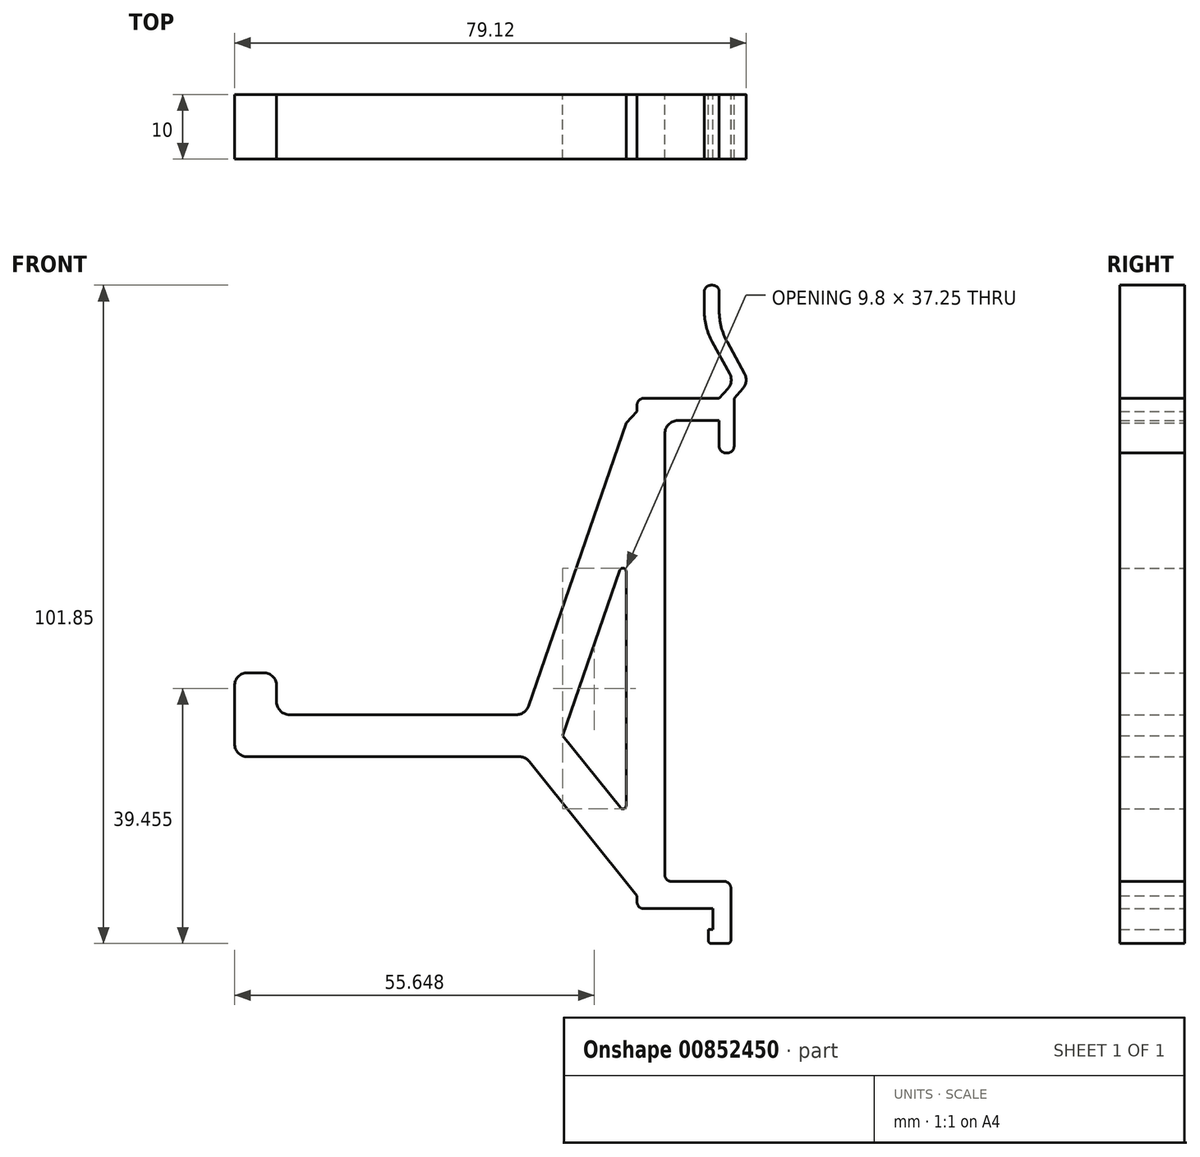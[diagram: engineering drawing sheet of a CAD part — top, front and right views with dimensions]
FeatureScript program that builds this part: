
annotation { "Feature Type Name" : "Feature", "Feature Type Description" : "" }
export const myFeature = defineFeature(function(context is Context, id is Id, definition is map)
    precondition{}
    {
        {
            var Q0;
            Q0=qCreatedBy(makeId("Front.planeOp"),FACE);
            var sketch = newSketch(context, id + "F0", { "sketchPlane" : qUnion([Q0])});
            skLineSegment(sketch, "E0", {"start": v(-6, -23.42) * mm, "end": v(-6, 12.84) * mm});
            skLineSegment(sketch, "E1", {"start": v(-6, 35.78) * mm, "end": v(-4.3, 37.6) * mm});
            skLineSegment(sketch, "E2", {"start": v(-4.3, 37.6) * mm, "end": v(-4.3, 38.6) * mm});
            skLineSegment(sketch, "E3", {"start": v(-3.3, 39.6) * mm, "end": v(8.4, 39.6) * mm});
            skLineSegment(sketch, "E4", {"start": v(10.7, 39.6) * mm, "end": v(10.7, 32.15) * mm});
            skLineSegment(sketch, "E5", {"start": v(9.7, 31.15) * mm, "end": v(9.4, 31.15) * mm});
            skLineSegment(sketch, "E6", {"start": v(8.4, 32.15) * mm, "end": v(8.4, 36.15) * mm});
            skLineSegment(sketch, "E7", {"start": v(8.4, 36.15) * mm, "end": v(2, 36.15) * mm});
            skLineSegment(sketch, "E8", {"start": v(0, 34.15) * mm, "end": v(0, -34.15) * mm});
            skLineSegment(sketch, "E9", {"start": v(1, -35.15) * mm, "end": v(9.2, -35.15) * mm});
            skLineSegment(sketch, "E10", {"start": v(10.2, -36.15) * mm, "end": v(10.2, -44.25) * mm});
            skLineSegment(sketch, "E11", {"start": v(9.7, -44.75) * mm, "end": v(7.2, -44.75) * mm});
            skLineSegment(sketch, "E12", {"start": v(6.7, -44.25) * mm, "end": v(6.7, -42.55) * mm});
            skLineSegment(sketch, "E13", {"start": v(6.7, -42.55) * mm, "end": v(7.45, -42.55) * mm});
            skLineSegment(sketch, "E14", {"start": v(7.45, -42.55) * mm, "end": v(7.45, -39.35) * mm});
            skLineSegment(sketch, "E15", {"start": v(7.45, -39.35) * mm, "end": v(-3.3, -39.35) * mm});
            skLineSegment(sketch, "E16", {"start": v(-4.3, -38.35) * mm, "end": v(-4.3, -37.35) * mm});
            skLineSegment(sketch, "E17", {"start": v(8.4, 56.1) * mm, "end": v(8.4, 53.14) * mm});
            skLineSegment(sketch, "E18", {"start": v(9.63, 48.34) * mm, "end": v(12.32, 43.41) * mm});
            skLineSegment(sketch, "E19", {"start": v(12.06, 41.12) * mm, "end": v(10.7, 39.6) * mm});
            skLineSegment(sketch, "E20", {"start": v(7.4, 57.1) * mm, "end": v(7.1, 57.1) * mm});
            skLineSegment(sketch, "E21", {"start": v(6.1, 56.1) * mm, "end": v(6.1, 53.14) * mm});
            skLineSegment(sketch, "E22", {"start": v(7.33, 48.34) * mm, "end": v(10.02, 43.41) * mm});
            skLineSegment(sketch, "E23", {"start": v(9.76, 41.12) * mm, "end": v(8.4, 39.6) * mm});
            skPoint(sketch, "E24.visualSharp", {"position": v(6.1, 50.58) * mm});
            skArc(sketch, "E24.filletArc", {"start": v(6.1, 53.14) * mm, "mid": v(6.41, 50.66) * mm, "end": v(7.33, 48.34) * mm});
            skPoint(sketch, "E25.visualSharp", {"position": v(8.4, 50.58) * mm});
            skArc(sketch, "E25.filletArc", {"start": v(8.4, 53.14) * mm, "mid": v(8.71, 50.66) * mm, "end": v(9.63, 48.34) * mm});
            skPoint(sketch, "E26.visualSharp", {"position": v(10.7, 42.17) * mm});
            skArc(sketch, "E26.filletArc", {"start": v(9.76, 41.12) * mm, "mid": v(10.25, 42.22) * mm, "end": v(10.02, 43.41) * mm});
            skPoint(sketch, "E27.visualSharp", {"position": v(13, 42.17) * mm});
            skArc(sketch, "E27.filletArc", {"start": v(12.06, 41.12) * mm, "mid": v(12.55, 42.22) * mm, "end": v(12.32, 43.41) * mm});
            skPoint(sketch, "E28.visualSharp", {"position": v(8.4, 57.1) * mm});
            skArc(sketch, "E28.filletArc", {"start": v(8.4, 56.1) * mm, "mid": v(8.1, 56.8) * mm, "end": v(7.4, 57.1) * mm});
            skPoint(sketch, "E29.visualSharp", {"position": v(6.1, 57.1) * mm});
            skArc(sketch, "E29.filletArc", {"start": v(7.1, 57.1) * mm, "mid": v(6.4, 56.8) * mm, "end": v(6.1, 56.1) * mm});
            skPoint(sketch, "E30.visualSharp", {"position": v(10.7, 31.15) * mm});
            skArc(sketch, "E30.filletArc", {"start": v(9.7, 31.15) * mm, "mid": v(10.4, 31.44) * mm, "end": v(10.7, 32.15) * mm});
            skPoint(sketch, "E31.visualSharp", {"position": v(8.4, 31.15) * mm});
            skArc(sketch, "E31.filletArc", {"start": v(8.4, 32.15) * mm, "mid": v(8.7, 31.44) * mm, "end": v(9.4, 31.15) * mm});
            skPoint(sketch, "E32.visualSharp", {"position": v(-4.3, 39.6) * mm});
            skArc(sketch, "E32.filletArc", {"start": v(-3.3, 39.6) * mm, "mid": v(-4, 39.3) * mm, "end": v(-4.3, 38.6) * mm});
            skPoint(sketch, "E33.visualSharp", {"position": v(-4.3, -39.35) * mm});
            skArc(sketch, "E33.filletArc", {"start": v(-4.3, -38.35) * mm, "mid": v(-4, -39.06) * mm, "end": v(-3.3, -39.35) * mm});
            skPoint(sketch, "E34.visualSharp", {"position": v(10.2, -35.15) * mm});
            skArc(sketch, "E34.filletArc", {"start": v(10.2, -36.15) * mm, "mid": v(9.9, -35.44) * mm, "end": v(9.2, -35.15) * mm});
            skLineSegment(sketch, "E35", {"start": v(-6, 35.78) * mm, "end": v(-21.09, -8) * mm});
            skLineSegment(sketch, "E36", {"start": v(-22.98, -9.35) * mm, "end": v(-58.05, -9.35) * mm});
            skLineSegment(sketch, "E37", {"start": v(-64.55, -15.85) * mm, "end": v(-22.5, -15.85) * mm});
            skLineSegment(sketch, "E38", {"start": v(-20.95, -16.6) * mm, "end": v(-4.3, -37.35) * mm});
            skLineSegment(sketch, "E39", {"start": v(-15.8, -12.63) * mm, "end": v(-6.97, 13) * mm});
            skLineSegment(sketch, "E40", {"start": v(-15.8, -12.63) * mm, "end": v(-6.89, -23.74) * mm});
            skLineSegment(sketch, "E41.top", {"start": v(-64.55, -2.85) * mm, "end": v(-62.05, -2.85) * mm});
            skLineSegment(sketch, "E41.left", {"start": v(-66.55, -13.85) * mm, "end": v(-66.55, -4.85) * mm});
            skLineSegment(sketch, "E41.right", {"start": v(-60.05, -7.35) * mm, "end": v(-60.05, -4.85) * mm});
            skPoint(sketch, "E42.visualSharp", {"position": v(-66.55, -15.85) * mm});
            skArc(sketch, "E42.filletArc", {"start": v(-66.55, -13.85) * mm, "mid": v(-65.96, -15.26) * mm, "end": v(-64.55, -15.85) * mm});
            skPoint(sketch, "E43.visualSharp", {"position": v(-60.05, -9.35) * mm});
            skArc(sketch, "E43.filletArc", {"start": v(-60.05, -7.35) * mm, "mid": v(-59.46, -8.76) * mm, "end": v(-58.05, -9.35) * mm});
            skPoint(sketch, "E44.visualSharp", {"position": v(-60.05, -2.85) * mm});
            skArc(sketch, "E44.filletArc", {"start": v(-60.05, -4.85) * mm, "mid": v(-60.64, -3.44) * mm, "end": v(-62.05, -2.85) * mm});
            skPoint(sketch, "E45.visualSharp", {"position": v(-66.55, -2.85) * mm});
            skArc(sketch, "E45.filletArc", {"start": v(-64.55, -2.85) * mm, "mid": v(-65.96, -3.44) * mm, "end": v(-66.55, -4.85) * mm});
            skPoint(sketch, "E46.visualSharp", {"position": v(-21.55, -9.35) * mm});
            skArc(sketch, "E46.filletArc", {"start": v(-22.98, -9.35) * mm, "mid": v(-21.82, -8.98) * mm, "end": v(-21.09, -8) * mm});
            skPoint(sketch, "E47.visualSharp", {"position": v(-21.55, -15.85) * mm});
            skArc(sketch, "E47.filletArc", {"start": v(-20.95, -16.6) * mm, "mid": v(-21.64, -16.05) * mm, "end": v(-22.5, -15.85) * mm});
            skPoint(sketch, "E48.visualSharp", {"position": v(-6, -24.84) * mm});
            skArc(sketch, "E48.filletArc", {"start": v(-6.89, -23.74) * mm, "mid": v(-6.33, -23.9) * mm, "end": v(-6, -23.42) * mm});
            skPoint(sketch, "E49.visualSharp", {"position": v(-6, 15.83) * mm});
            skArc(sketch, "E49.filletArc", {"start": v(-6, 12.84) * mm, "mid": v(-6.42, 13.33) * mm, "end": v(-6.97, 13) * mm});
            skPoint(sketch, "E50.visualSharp", {"position": v(0, -35.15) * mm});
            skArc(sketch, "E50.filletArc", {"start": v(0, -34.15) * mm, "mid": v(0.3, -34.86) * mm, "end": v(1, -35.15) * mm});
            skPoint(sketch, "E51.visualSharp", {"position": v(0, 36.15) * mm});
            skArc(sketch, "E51.filletArc", {"start": v(2, 36.15) * mm, "mid": v(0.59, 35.56) * mm, "end": v(0, 34.15) * mm});
            skPoint(sketch, "E52.visualSharp", {"position": v(6.7, -44.75) * mm});
            skArc(sketch, "E52.filletArc", {"start": v(6.7, -44.25) * mm, "mid": v(6.85, -44.6) * mm, "end": v(7.2, -44.75) * mm});
            skPoint(sketch, "E53.visualSharp", {"position": v(10.2, -44.75) * mm});
            skArc(sketch, "E53.filletArc", {"start": v(9.7, -44.75) * mm, "mid": v(10.05, -44.6) * mm, "end": v(10.2, -44.25) * mm});
            skSolve(sketch);
        }
        {
            var Q0;
            Q0=qSketchRegion(id+"F0",true);
            extrude(context, id + "F1", {"entities" : qUnion([Q0]), "offsetDistance" : 25 * mm, "depth" : 10 * mm, "symmetric" : true});
        }
    });
